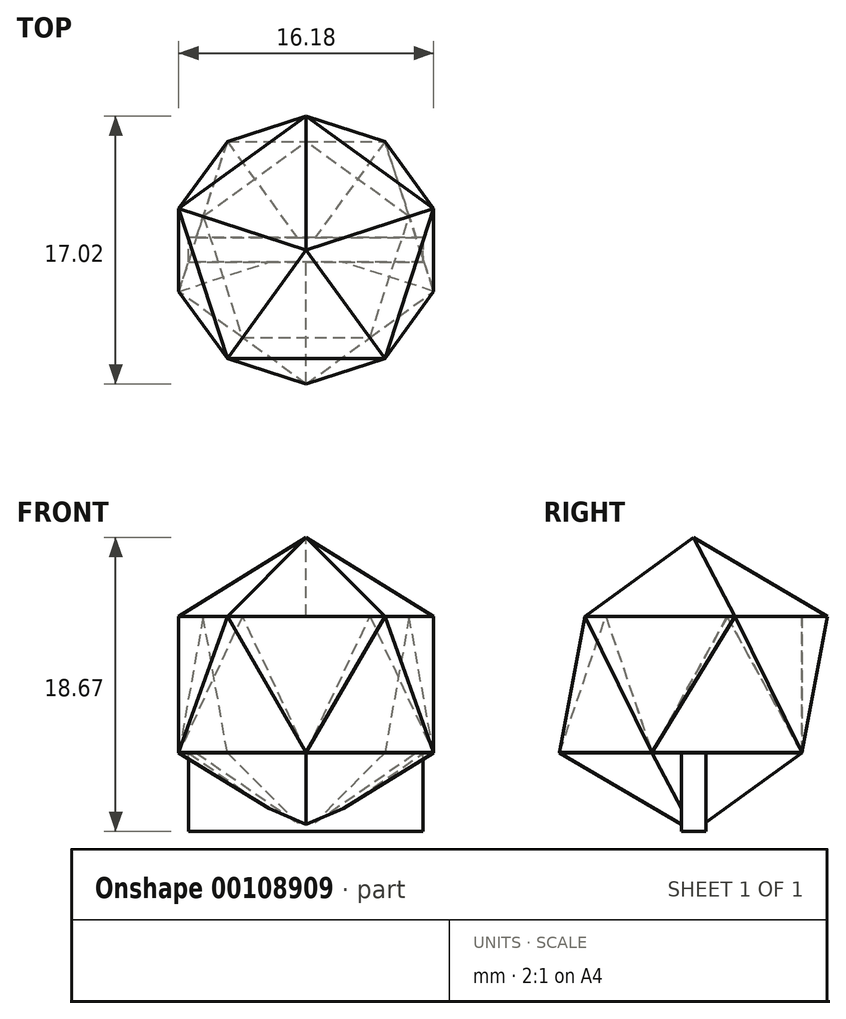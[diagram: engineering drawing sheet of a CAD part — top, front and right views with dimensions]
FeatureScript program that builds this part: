
annotation { "Feature Type Name" : "Feature", "Feature Type Description" : "" }
export const myFeature = defineFeature(function(context is Context, id is Id, definition is map)
    precondition{}
    {
        {
            var Q0;
            Q0=qCreatedBy(makeId("Top.planeOp"),FACE);
            var sketch = newSketch(context, id + "F0", { "sketchPlane" : qUnion([Q0])});
            skCircle(sketch, "E0.cCircle", {"center": v(0, 0) * mm, "radius": 6.88 * mm, "construction": true});
            skLineSegment(sketch, "E0.0", {"start": v(5, -6.88) * mm, "end": v(-5, -6.88) * mm});
            skLineSegment(sketch, "E0.1", {"start": v(-5, -6.88) * mm, "end": v(-8.1, 2.63) * mm});
            skLineSegment(sketch, "E0.2", {"start": v(-8.1, 2.63) * mm, "end": v(0, 8.5) * mm});
            skLineSegment(sketch, "E0.3", {"start": v(0, 8.5) * mm, "end": v(8.1, 2.63) * mm});
            skLineSegment(sketch, "E0.4", {"start": v(8.1, 2.63) * mm, "end": v(5, -6.88) * mm});
            skPoint(sketch, "E0.0.midPoint", {"position": v(0, -6.88) * mm});
            skLineSegment(sketch, "E1", {"start": v(-5, -6.88) * mm, "end": v(0, 0) * mm});
            skSolve(sketch);
        }
        {
            var Q0;
            Q0=qCreatedBy(makeId("Top.planeOp"),FACE);
            cPlane(context, id + "F1", {"entities" : qUnion([Q0]), "cplaneType" : CPlaneType.OFFSET, "offset" : 5 * mm, "width" : 150 * mm, "height" : 150 * mm});
        }
        {
            var Q0;
            Q0=qCreatedBy(id+"F1.planeOp",FACE);
            var sketch = newSketch(context, id + "F2", { "sketchPlane" : qUnion([Q0])});
            skPoint(sketch, "E2", {"position": v(0, 0) * mm});
            skSolve(sketch);
        }
        {
            var Q0;
            Q0=makeQuery(id+"F0.imprint","IMPRINT",FACE,{"disambiguationData":[TD([[makeQuery(id+"F0.imprint","IMPRINT",EDGE,{"derivedFrom":sQuery(id+"F0.wireOp",EDGE,"E0.0")}),-1.0]])]});
            var Q1;
            Q1=sQuery(id+"F2.wireOp",VERTEX,"E2");
            loft(context, id + "F3", {"sheetProfilesArray" : [{ "sheetProfileEntities" : qUnion([Q0]) }, { "sheetProfileEntities" : qUnion([Q1]) }]});
        }
        {
            var Q0;
            Q0=makeQuery(id+"F0.imprint","IMPRINT",FACE,{"disambiguationData":[TD([[makeQuery(id+"F0.imprint","IMPRINT",EDGE,{"derivedFrom":sQuery(id+"F0.wireOp",EDGE,"E0.0")}),-1.0]])]});
            cPlane(context, id + "F4", {"entities" : qUnion([Q0]), "cplaneType" : CPlaneType.OFFSET, "offset" : 8.66 * mm, "oppositeDirection" : true, "width" : 150 * mm, "height" : 150 * mm});
        }
        {
            var Q0;
            Q0=qCreatedBy(id+"F4.planeOp",FACE);
            var sketch = newSketch(context, id + "F5", { "sketchPlane" : qUnion([Q0])});
            skCircle(sketch, "E3.cCircle", {"center": v(0, 0) * mm, "radius": 6.88 * mm, "construction": true});
            skLineSegment(sketch, "E3.0", {"start": v(8.1, -2.63) * mm, "end": v(0, -8.5) * mm});
            skLineSegment(sketch, "E3.1", {"start": v(0, -8.5) * mm, "end": v(-8.09, -2.63) * mm});
            skLineSegment(sketch, "E3.2", {"start": v(-8.09, -2.63) * mm, "end": v(-5, 6.88) * mm});
            skLineSegment(sketch, "E3.3", {"start": v(-5, 6.88) * mm, "end": v(5, 6.88) * mm});
            skLineSegment(sketch, "E3.4", {"start": v(5, 6.88) * mm, "end": v(8.1, -2.63) * mm});
            skPoint(sketch, "E3.0.midPoint", {"position": v(4.05, -5.57) * mm});
            skSolve(sketch);
        }
        {
            var Q0;
            Q0=makeQuery(id+"F5.imprint","IMPRINT",FACE,{"disambiguationData":[TD([[makeQuery(id+"F5.imprint","IMPRINT",EDGE,{"derivedFrom":sQuery(id+"F5.wireOp",EDGE,"E3.0")}),-1.0]])]});
            extrude(context, id + "F6", {"entities" : qUnion([Q0]), "oppositeDirection" : true, "depth" : 0.01 * mm});
        }
        {
            var Q0;
            Q0=makeQuery(id+"F6.opExtrude","SWEPT_FACE",FACE,{"disambiguationData":[OSD([sQuery(id+"F5.wireOp",EDGE,"E3.2")])]});
            var sketch = newSketch(context, id + "F7", { "sketchPlane" : qUnion([Q0])});
            skPoint(sketch, "E4", {"position": v(-0.02, -0.03) * mm});
            skLineSegment(sketch, "E5", {"start": v(-5, -8.66) * mm, "end": v(-0.02, -0.03) * mm});
            skLineSegment(sketch, "E6", {"start": v(-0.02, -0.03) * mm, "end": v(5, -8.66) * mm});
            skSolve(sketch);
        }
        {
            var Q0;
            Q0=makeQuery(id+"F7.imprint","IMPRINT",FACE,{"disambiguationData":[TD([[makeQuery(id+"F7.imprint","IMPRINT",EDGE,{"derivedFrom":sQuery(id+"F7.wireOp",EDGE,"E5")}),-1.0]])]});
            var Q1;
            Q1=makeQuery(id+"F3.opLoft","MID_CAP_VERTEX",VERTEX,{"disambiguationData":[OSD([sQuery(id+"F0.wireOp",EDGE,"E0.1"),sQuery(id+"F0.wireOp",EDGE,"E0.2")])],"capPos":0.0});
            loft(context, id + "F8", {"sheetProfilesArray" : [{ "sheetProfileEntities" : qUnion([Q0]) }, { "sheetProfileEntities" : qUnion([Q1]) }]});
        }
        {
            var Q0;
            Q0=makeQuery(id+"F6.opExtrude","SWEPT_FACE",FACE,{"disambiguationData":[OSD([sQuery(id+"F5.wireOp",EDGE,"E3.1")])]});
            var sketch = newSketch(context, id + "F9", { "sketchPlane" : qUnion([Q0])});
            skLineSegment(sketch, "E7", {"start": v(0, 0) * mm, "end": v(-5, -8.66) * mm});
            skLineSegment(sketch, "E8", {"start": v(-5, -8.66) * mm, "end": v(5, -8.66) * mm});
            skLineSegment(sketch, "E9", {"start": v(5, -8.66) * mm, "end": v(0, 0) * mm});
            skSolve(sketch);
        }
        {
            var Q1;
            Q1=makeQuery(id+"F9.imprint","IMPRINT",FACE,{"disambiguationData":[TD([[makeQuery(id+"F9.imprint","IMPRINT",EDGE,{"derivedFrom":sQuery(id+"F9.wireOp",EDGE,"E7")}),1.0]])]});
            var Q2;
            Q2=makeQuery(id+"F3.opLoft","MID_CAP_VERTEX",VERTEX,{"disambiguationData":[OSD([sQuery(id+"F0.wireOp",EDGE,"E0.0"),sQuery(id+"F0.wireOp",EDGE,"E0.1")])],"capPos":0.0});
            loft(context, id + "F10", {"operationType" : NewBodyOperationType.ADD, "sheetProfilesArray" : [{ "sheetProfileEntities" : qUnion([Q1]) }, { "sheetProfileEntities" : qUnion([Q2]) }]});
        }
        {
            var Q0;
            Q0=makeQuery(id+"F8.opLoft","SWEPT_FACE",FACE,{"disambiguationData":[OSD([sQuery(id+"F5.wireOp",EDGE,"E3.1"),sQuery(id+"F5.wireOp",EDGE,"E3.2"),sQuery(id+"F7.wireOp",EDGE,"E5"),sQuery(id+"F7.wireOp",EDGE,"E6")])]});
            var Q1;
            Q1=makeQuery(id+"F10.opLoft","SWEPT_FACE",FACE,{"disambiguationData":[OSD([sQuery(id+"F5.wireOp",EDGE,"E3.1"),sQuery(id+"F5.wireOp",EDGE,"E3.2"),sQuery(id+"F9.wireOp",EDGE,"E7"),sQuery(id+"F9.wireOp",EDGE,"E8"),sQuery(id+"F9.wireOp",EDGE,"E9")])]});
            loft(context, id + "F11", {"sheetProfilesArray" : [{ "sheetProfileEntities" : qUnion([Q0]) }, { "sheetProfileEntities" : qUnion([Q1]) }]});
        }
        {
            var Q0;
            Q0=makeQuery(id+"F6.opExtrude","SWEPT_FACE",FACE,{"disambiguationData":[OSD([sQuery(id+"F5.wireOp",EDGE,"E3.3")])]});
            var sketch = newSketch(context, id + "F12", { "sketchPlane" : qUnion([Q0])});
            skLineSegment(sketch, "E10", {"start": v(0, 0) * mm, "end": v(-5, -8.66) * mm});
            skLineSegment(sketch, "E11", {"start": v(-5, -8.66) * mm, "end": v(5, -8.66) * mm});
            skLineSegment(sketch, "E12", {"start": v(5, -8.66) * mm, "end": v(0, 0) * mm});
            skSolve(sketch);
        }
        {
            var Q1;
            Q1=makeQuery(id+"F12.imprint","IMPRINT",FACE,{"disambiguationData":[TD([[makeQuery(id+"F12.imprint","IMPRINT",EDGE,{"derivedFrom":sQuery(id+"F12.wireOp",EDGE,"E10")}),1.0]])]});
            var Q2;
            Q2=makeQuery(id+"F3.opLoft","MID_CAP_VERTEX",VERTEX,{"disambiguationData":[OSD([sQuery(id+"F0.wireOp",EDGE,"E0.2"),sQuery(id+"F0.wireOp",EDGE,"E0.3")])],"capPos":0.0});
            loft(context, id + "F13", {"operationType" : NewBodyOperationType.ADD, "sheetProfilesArray" : [{ "sheetProfileEntities" : qUnion([Q1]) }, { "sheetProfileEntities" : qUnion([Q2]) }]});
        }
        {
            var Q0;
            Q0=makeQuery(id+"F8.opLoft","SWEPT_FACE",FACE,{"disambiguationData":[OSD([sQuery(id+"F5.wireOp",EDGE,"E3.2"),sQuery(id+"F5.wireOp",EDGE,"E3.3"),sQuery(id+"F7.wireOp",EDGE,"E5"),sQuery(id+"F7.wireOp",EDGE,"E6")])]});
            var Q1;
            Q1=makeQuery(id+"F13.opLoft","SWEPT_FACE",FACE,{"disambiguationData":[OSD([sQuery(id+"F5.wireOp",EDGE,"E3.2"),sQuery(id+"F5.wireOp",EDGE,"E3.3"),sQuery(id+"F12.wireOp",EDGE,"E10"),sQuery(id+"F12.wireOp",EDGE,"E11"),sQuery(id+"F12.wireOp",EDGE,"E12")])]});
            loft(context, id + "F14", {"sheetProfilesArray" : [{ "sheetProfileEntities" : qUnion([Q0]) }, { "sheetProfileEntities" : qUnion([Q1]) }]});
        }
        {
            var Q0;
            Q0=makeQuery(id+"F6.opExtrude","SWEPT_FACE",FACE,{"disambiguationData":[OSD([sQuery(id+"F5.wireOp",EDGE,"E3.0")])]});
            var sketch = newSketch(context, id + "F15", { "sketchPlane" : qUnion([Q0])});
            skLineSegment(sketch, "E13", {"start": v(-5, -8.66) * mm, "end": v(0, -0.02) * mm});
            skLineSegment(sketch, "E14", {"start": v(0, -0.02) * mm, "end": v(5, -8.66) * mm});
            skLineSegment(sketch, "E15", {"start": v(5, -8.66) * mm, "end": v(-5, -8.66) * mm});
            skSolve(sketch);
        }
        {
            var Q0;
            Q0=makeQuery(id+"F3.opLoft","MID_CAP_VERTEX",VERTEX,{"disambiguationData":[OSD([sQuery(id+"F0.wireOp",EDGE,"E0.0"),sQuery(id+"F0.wireOp",EDGE,"E0.4")])],"capPos":0.0});
            var Q1;
            Q1=makeQuery(id+"F15.imprint","IMPRINT",FACE,{"disambiguationData":[TD([[makeQuery(id+"F15.imprint","IMPRINT",EDGE,{"derivedFrom":sQuery(id+"F15.wireOp",EDGE,"E13")}),-1.0]])]});
            loft(context, id + "F16", {"sheetProfilesArray" : [{ "sheetProfileEntities" : qUnion([Q0]) }, { "sheetProfileEntities" : qUnion([Q1]) }]});
        }
        {
            var Q0;
            Q0=makeQuery(id+"F10.opLoft","SWEPT_FACE",FACE,{"disambiguationData":[OSD([sQuery(id+"F5.wireOp",EDGE,"E3.0"),sQuery(id+"F5.wireOp",EDGE,"E3.1"),sQuery(id+"F9.wireOp",EDGE,"E7"),sQuery(id+"F9.wireOp",EDGE,"E8"),sQuery(id+"F9.wireOp",EDGE,"E9")])]});
            var Q1;
            Q1=makeQuery(id+"F16.opLoft","SWEPT_FACE",FACE,{"disambiguationData":[OSD([sQuery(id+"F5.wireOp",EDGE,"E3.0"),sQuery(id+"F5.wireOp",EDGE,"E3.1"),sQuery(id+"F15.wireOp",EDGE,"E13"),sQuery(id+"F15.wireOp",EDGE,"E14"),sQuery(id+"F15.wireOp",EDGE,"E15")])]});
            loft(context, id + "F17", {"sheetProfilesArray" : [{ "sheetProfileEntities" : qUnion([Q0]) }, { "sheetProfileEntities" : qUnion([Q1]) }]});
        }
        {
            var Q0;
            Q0=makeQuery(id+"F6.opExtrude","SWEPT_FACE",FACE,{"disambiguationData":[OSD([sQuery(id+"F5.wireOp",EDGE,"E3.4")])]});
            var sketch = newSketch(context, id + "F18", { "sketchPlane" : qUnion([Q0])});
            skLineSegment(sketch, "E16", {"start": v(-5, -8.66) * mm, "end": v(0, -0.02) * mm});
            skLineSegment(sketch, "E17", {"start": v(0, -0.02) * mm, "end": v(5, -8.66) * mm});
            skLineSegment(sketch, "E18", {"start": v(5, -8.66) * mm, "end": v(-5, -8.66) * mm});
            skSolve(sketch);
        }
        {
            var Q0;
            Q0=makeQuery(id+"F18.imprint","IMPRINT",FACE,{"disambiguationData":[TD([[makeQuery(id+"F18.imprint","IMPRINT",EDGE,{"derivedFrom":sQuery(id+"F18.wireOp",EDGE,"E16")}),-1.0]])]});
            var Q1;
            Q1=makeQuery(id+"F3.opLoft","MID_CAP_VERTEX",VERTEX,{"disambiguationData":[OSD([sQuery(id+"F0.wireOp",EDGE,"E0.3"),sQuery(id+"F0.wireOp",EDGE,"E0.4")])],"capPos":0.0});
            loft(context, id + "F19", {"sheetProfilesArray" : [{ "sheetProfileEntities" : qUnion([Q0]) }, { "sheetProfileEntities" : qUnion([Q1]) }]});
        }
        {
            var Q0;
            Q0=makeQuery(id+"F16.opLoft","SWEPT_FACE",FACE,{"disambiguationData":[OSD([sQuery(id+"F5.wireOp",EDGE,"E3.0"),sQuery(id+"F5.wireOp",EDGE,"E3.4"),sQuery(id+"F15.wireOp",EDGE,"E13"),sQuery(id+"F15.wireOp",EDGE,"E14"),sQuery(id+"F15.wireOp",EDGE,"E15")])]});
            var Q1;
            Q1=makeQuery(id+"F19.opLoft","SWEPT_FACE",FACE,{"disambiguationData":[OSD([sQuery(id+"F5.wireOp",EDGE,"E3.0"),sQuery(id+"F5.wireOp",EDGE,"E3.4"),sQuery(id+"F18.wireOp",EDGE,"E16"),sQuery(id+"F18.wireOp",EDGE,"E17"),sQuery(id+"F18.wireOp",EDGE,"E18")])]});
            loft(context, id + "F20", {"sheetProfilesArray" : [{ "sheetProfileEntities" : qUnion([Q0]) }, { "sheetProfileEntities" : qUnion([Q1]) }]});
        }
        {
            var Q0;
            Q0=makeQuery(id+"F19.opLoft","SWEPT_FACE",FACE,{"disambiguationData":[OSD([sQuery(id+"F5.wireOp",EDGE,"E3.3"),sQuery(id+"F5.wireOp",EDGE,"E3.4"),sQuery(id+"F18.wireOp",EDGE,"E16"),sQuery(id+"F18.wireOp",EDGE,"E17"),sQuery(id+"F18.wireOp",EDGE,"E18")])]});
            var sketch = newSketch(context, id + "F21", { "sketchPlane" : qUnion([Q0])});
            skLineSegment(sketch, "E19", {"start": v(-5.18, -10.98) * mm, "end": v(-8.4, -1.37) * mm});
            skLineSegment(sketch, "E20", {"start": v(-8.4, -1.37) * mm, "end": v(-6.79, -1.13) * mm});
            skLineSegment(sketch, "E21", {"start": v(-6.79, -1.13) * mm, "end": v(-5.18, -10.98) * mm});
            skSolve(sketch);
        }
        {
            var Q0;
            Q0=makeQuery(id+"F21.imprint","IMPRINT",FACE,{"disambiguationData":[TD([[makeQuery(id+"F21.imprint","IMPRINT",EDGE,{"derivedFrom":sQuery(id+"F21.wireOp",EDGE,"E19")}),-1.0]])]});
            var Q1;
            Q1=makeQuery(id+"F13.opLoft","SWEPT_FACE",FACE,{"disambiguationData":[OSD([sQuery(id+"F5.wireOp",EDGE,"E3.3"),sQuery(id+"F5.wireOp",EDGE,"E3.4"),sQuery(id+"F12.wireOp",EDGE,"E10"),sQuery(id+"F12.wireOp",EDGE,"E11"),sQuery(id+"F12.wireOp",EDGE,"E12")])]});
            loft(context, id + "F22", {"sheetProfilesArray" : [{ "sheetProfileEntities" : qUnion([Q0]) }, { "sheetProfileEntities" : qUnion([Q1]) }]});
        }
        {
            var Q0;
            Q0=makeQuery(id+"F6.opExtrude","CAP_FACE",FACE,{"disambiguationData":[OSD([sQuery(id+"F5.wireOp",EDGE,"E3.0"),sQuery(id+"F5.wireOp",EDGE,"E3.1"),sQuery(id+"F5.wireOp",EDGE,"E3.2"),sQuery(id+"F5.wireOp",EDGE,"E3.3"),sQuery(id+"F5.wireOp",EDGE,"E3.4")])],"isStart":false});
            cPlane(context, id + "F23", {"entities" : qUnion([Q0]), "cplaneType" : CPlaneType.OFFSET, "offset" : 5 * mm, "width" : 150 * mm, "height" : 150 * mm});
        }
        {
            var Q0;
            Q0=qCreatedBy(id+"F23.planeOp",FACE);
            var sketch = newSketch(context, id + "F24", { "sketchPlane" : qUnion([Q0])});
            skPoint(sketch, "E22", {"position": v(0, 0) * mm});
            skSolve(sketch);
        }
        {
            var Q1;
            Q1=makeQuery(id+"F6.opExtrude","CAP_FACE",FACE,{"disambiguationData":[OSD([sQuery(id+"F5.wireOp",EDGE,"E3.0"),sQuery(id+"F5.wireOp",EDGE,"E3.1"),sQuery(id+"F5.wireOp",EDGE,"E3.2"),sQuery(id+"F5.wireOp",EDGE,"E3.3"),sQuery(id+"F5.wireOp",EDGE,"E3.4")])],"isStart":false});
            var Q2;
            Q2=sQuery(id+"F24.wireOp",VERTEX,"E22");
            loft(context, id + "F25", {"operationType" : NewBodyOperationType.ADD, "sheetProfilesArray" : [{ "sheetProfileEntities" : qUnion([Q1]) }, { "sheetProfileEntities" : qUnion([Q2]) }]});
        }
        {
            var Q0;
            Q0=qCreatedBy(id+"F23.planeOp",FACE);
            cPlane(context, id + "F26", {"entities" : qUnion([Q0]), "cplaneType" : CPlaneType.OFFSET, "offset" : 5 * mm, "oppositeDirection" : true, "width" : 150 * mm, "height" : 150 * mm});
        }
        {
            var Q0;
            Q0=qCreatedBy(id+"F26.planeOp",FACE);
            var sketch = newSketch(context, id + "F27", { "sketchPlane" : qUnion([Q0])});
            skPoint(sketch, "E23.middle", {"position": v(0, 0) * mm});
            skLineSegment(sketch, "E24.bottom", {"start": v(7.44, 0.77) * mm, "end": v(-7.45, 0.77) * mm});
            skLineSegment(sketch, "E24.top", {"start": v(7.44, -0.78) * mm, "end": v(-7.45, -0.78) * mm});
            skLineSegment(sketch, "E24.left", {"start": v(7.44, 0.77) * mm, "end": v(7.44, -0.78) * mm});
            skLineSegment(sketch, "E24.right", {"start": v(-7.45, 0.77) * mm, "end": v(-7.45, -0.78) * mm});
            skSolve(sketch);
        }
        {
            var Q0;
            Q0=makeQuery(id+"F27.imprint","IMPRINT",FACE,{"disambiguationData":[TD([[makeQuery(id+"F27.imprint","IMPRINT",EDGE,{"derivedFrom":sQuery(id+"F27.wireOp",EDGE,"E24.bottom")}),1.0]])]});
            extrude(context, id + "F28", {"entities" : qUnion([Q0]), "operationType" : NewBodyOperationType.ADD, "depth" : 5 * mm});
        }
    });
